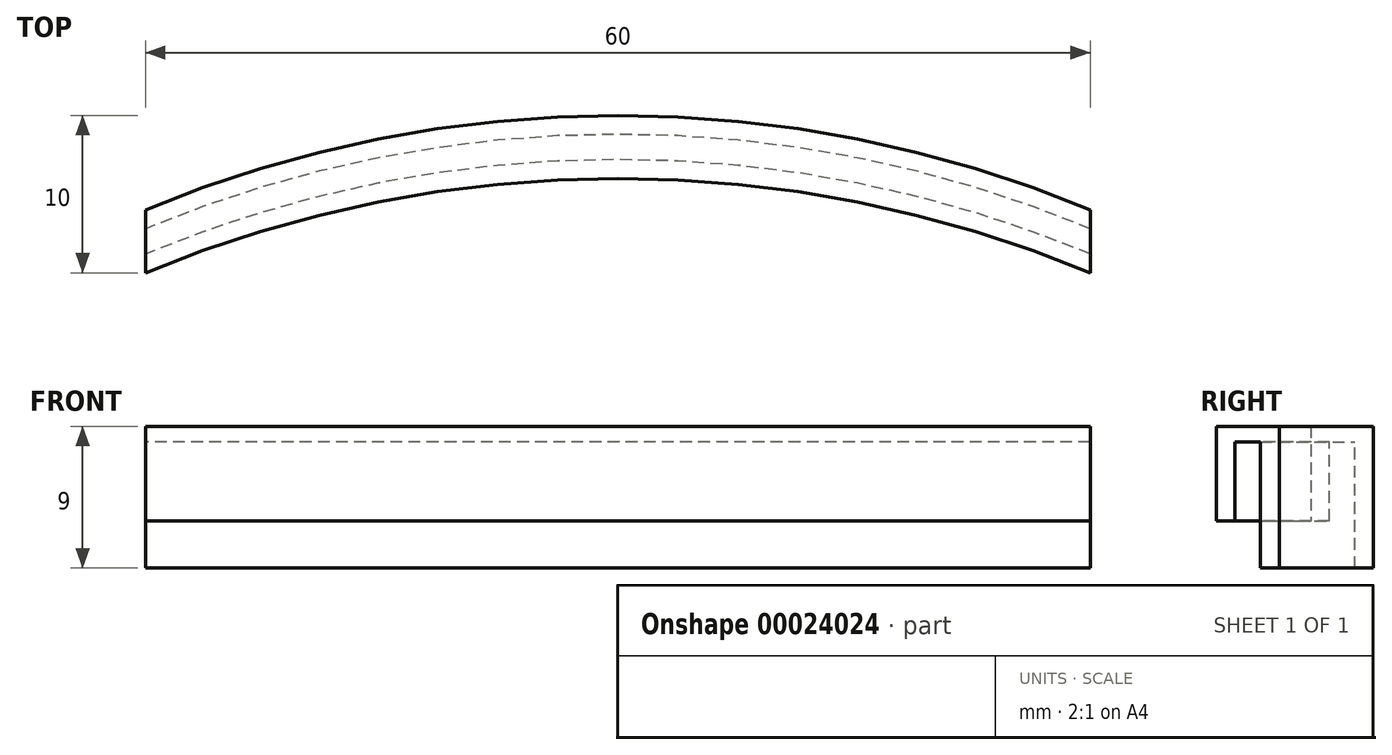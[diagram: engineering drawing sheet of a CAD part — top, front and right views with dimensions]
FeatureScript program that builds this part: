
annotation { "Feature Type Name" : "Feature", "Feature Type Description" : "" }
export const myFeature = defineFeature(function(context is Context, id is Id, definition is map)
    precondition{}
    {
        {
            var Q0;
            Q0=qCreatedBy(makeId("Top.planeOp"),FACE);
            var sketch = newSketch(context, id + "F0", { "sketchPlane" : qUnion([Q0])});
            skLineSegment(sketch, "E0", {"start": v(0, 0) * mm, "end": v(-60, 0) * mm, "construction": true});
            skLineSegment(sketch, "E1", {"start": v(-30, 0) * mm, "end": v(-30, 6) * mm, "construction": true});
            skPoint(sketch, "E1.endSnap0", {"position": v(-30, 0) * mm});
            skArc(sketch, "E2", {"start": v(0, 0) * mm, "mid": v(-30, 6) * mm, "end": v(-60, 0) * mm});
            skLineSegment(sketch, "E3", {"start": v(-60, 0) * mm, "end": v(-60, -1.2) * mm});
            skLineSegment(sketch, "E4", {"start": v(0, 0) * mm, "end": v(0, -1.2) * mm, "construction": true});
            skLineSegment(sketch, "E5", {"start": v(-60, -1.2) * mm, "end": v(-60, -2.8) * mm});
            skLineSegment(sketch, "E6", {"start": v(-60, -4) * mm, "end": v(-60, -2.8) * mm});
            skLineSegment(sketch, "E7", {"start": v(0, -4) * mm, "end": v(0, 0) * mm});
            skLineSegment(sketch, "E8", {"start": v(-30, 6) * mm, "end": v(-30, 4.8) * mm});
            skLineSegment(sketch, "E9.MirrorCS", {"start": v(0, -1.2) * mm, "end": v(0, -2.8) * mm, "construction": true});
            skArc(sketch, "E10", {"start": v(0, -1.2) * mm, "mid": v(-30, 4.8) * mm, "end": v(-60, -1.2) * mm});
            skLineSegment(sketch, "E11", {"start": v(-30, 4.8) * mm, "end": v(-30, 3.2) * mm, "construction": true});
            skArc(sketch, "E12", {"start": v(0, -2.8) * mm, "mid": v(-30, 3.2) * mm, "end": v(-60, -2.8) * mm});
            skLineSegment(sketch, "E13", {"start": v(-30, 3.2) * mm, "end": v(-30, 2) * mm, "construction": true});
            skArc(sketch, "E14", {"start": v(0, -4) * mm, "mid": v(-30, 2) * mm, "end": v(-60, -4) * mm});
            skSolve(sketch);
        }
        {
            var Q0;
            {var subQ0=sQuery(id+"F0.wireOp",EDGE,"E3");Q0=makeQuery(id+"F0.imprint","IMPRINT",FACE,{"disambiguationData":[TD([[makeQuery(id+"F0.imprint","IMPRINT",EDGE,{"derivedFrom":subQ0}),1.0]])]});}
            var Q1;
            {var subQ3=sQuery(id+"F0.wireOp",EDGE,"E8");Q1=makeQuery(id+"F0.imprint","IMPRINT",FACE,{"disambiguationData":[TD([[makeQuery(id+"F0.imprint","IMPRINT",EDGE,{"derivedFrom":subQ3}),1.0]])]});}
            var Q2;
            {var subQ1=sQuery(id+"F0.wireOp",EDGE,"E5");Q2=makeQuery(id+"F0.imprint","IMPRINT",FACE,{"disambiguationData":[TD([[makeQuery(id+"F0.imprint","IMPRINT",EDGE,{"derivedFrom":subQ1}),1.0]])]});}
            var Q3;
            Q3=makeQuery(id+"F0.imprint","IMPRINT",FACE,{"disambiguationData":[TD([[makeQuery(id+"F0.imprint","IMPRINT",EDGE,{"derivedFrom":sQuery(id+"F0.wireOp",EDGE,"E6")}),-1.0]])]});
            extrude(context, id + "F1", {"entities" : qUnion([Q0, Q1, Q2, Q3]), "depth" : 1 * mm});
        }
        {
            var Q0;
            {var subQ3=sQuery(id+"F0.wireOp",EDGE,"E8");Q0=makeQuery(id+"F0.imprint","IMPRINT",FACE,{"disambiguationData":[TD([[makeQuery(id+"F0.imprint","IMPRINT",EDGE,{"derivedFrom":subQ3}),1.0]])]});}
            var Q1;
            {var subQ0=sQuery(id+"F0.wireOp",EDGE,"E3");Q1=makeQuery(id+"F0.imprint","IMPRINT",FACE,{"disambiguationData":[TD([[makeQuery(id+"F0.imprint","IMPRINT",EDGE,{"derivedFrom":subQ0}),1.0]])]});}
            extrude(context, id + "F2", {"entities" : qUnion([Q0, Q1]), "operationType" : NewBodyOperationType.ADD, "oppositeDirection" : true, "depth" : 8 * mm});
        }
        {
            var Q0;
            Q0=makeQuery(id+"F0.imprint","IMPRINT",FACE,{"disambiguationData":[TD([[makeQuery(id+"F0.imprint","IMPRINT",EDGE,{"derivedFrom":sQuery(id+"F0.wireOp",EDGE,"E6")}),-1.0]])]});
            extrude(context, id + "F3", {"entities" : qUnion([Q0]), "operationType" : NewBodyOperationType.ADD, "oppositeDirection" : true, "depth" : 5 * mm});
        }
    });
